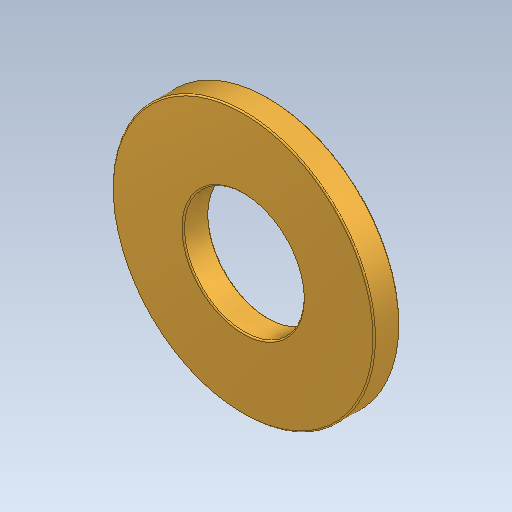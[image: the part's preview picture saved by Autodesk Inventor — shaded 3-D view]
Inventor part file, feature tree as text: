
AUTODESK INVENTOR PART (.ipt)
format: ipt  version: 2023 (Build 270158000, 158)  size: 133,120 bytes
history: native  units: in
note: dims shown in document units (in); Inventor stores cm internally (conversion verified against a paired STEP export)
features: fillet x1
ambient origin geometry x8: Origin, YZ Plane, XZ Plane, XY Plane, X Axis, Y Axis, Z Axis, Center Point
bodies: Solid1 (feature_tree)
feature tree (1):
  fillet  "Fillet1"  [1 undecoded]
note: 1 required parameter value undecoded (feature->parameter linkage not recoverable at this tier; creation-order binding heuristic only, values carry confidence <= 0.55)
